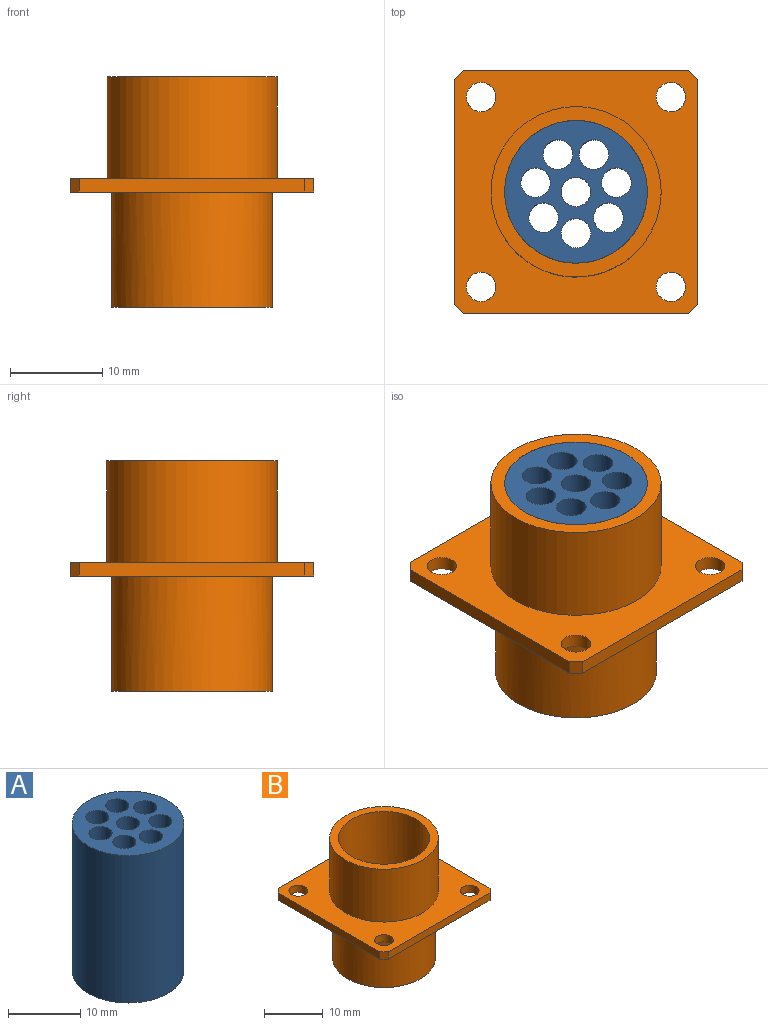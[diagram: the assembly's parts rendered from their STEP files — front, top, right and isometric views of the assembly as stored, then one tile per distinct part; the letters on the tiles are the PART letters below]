
ASSEMBLY  parts=2 mates=1
PART A: 11 faces, bbox 15.5x15.5x25 mm
  f0: cylinder r=7.75mm len=25mm, axis (0,0,1), area 1217.4mm2, adj f1,f10
  f1: plane 15.5x15.5mm, normal (0,0,-1), area 124.4mm2, adj f0,f2,f3,f4,f5,f6,f7,f8
  f2: cylinder r=1.6mm len=25mm, axis (0,0,1), area 251.3mm2, adj f1,f10
  f3: cylinder r=1.6mm len=25mm, axis (0,0,1), area 251.3mm2, adj f1,f10
  f4: cylinder r=1.6mm len=25mm, axis (0,0,1), area 251.3mm2, adj f1,f10
  f5: cylinder r=1.6mm len=25mm, axis (0,0,1), area 251.3mm2, adj f1,f10
  f6: cylinder r=1.6mm len=25mm, axis (0,0,1), area 251.3mm2, adj f1,f10
  f7: cylinder r=1.6mm len=25mm, axis (0,0,1), area 251.3mm2, adj f1,f10
  f8: cylinder r=1.6mm len=25mm, axis (0,0,1), area 251.3mm2, adj f1,f10
  f9: cylinder r=1.6mm len=25mm, axis (0,0,1), area 251.3mm2, adj f1,f10
  f10: plane 15.5x15.5mm, normal (0,0,1), area 124.4mm2, adj f0,f2,f3,f4,f5,f6,f7,f8
PART B: 19 faces, bbox 26.5x26.5x25 mm
  f0: plane 26.5x26.5mm, normal (0,0,-1), area 427.6mm2, adj f2,f3,f4,f5,f6,f7,f8,f9
  f1: plane 26.5x26.5mm, normal (0,0,1), area 399.3mm2, adj f2,f3,f4,f5,f6,f7,f8,f9
  f2: plane 24.5x1.5mm, normal (0,1,0), area 36.8mm2, adj f0,f1,f3,f9
  f3: plane 1.5x1mm, normal (0.71,0.71,0), area 2.1mm2, adj f0,f1,f2,f4
  f4: plane 24.5x1.5mm, normal (1,0,0), area 36.8mm2, adj f0,f1,f3,f5
  f5: plane 1.5x1mm, normal (0.71,-0.71,0), area 2.1mm2, adj f0,f1,f4,f6
  f6: plane 24.5x1.5mm, normal (0,-1,0), area 36.8mm2, adj f0,f1,f5,f7
  f7: plane 1.5x1mm, normal (-0.71,-0.71,0), area 2.1mm2, adj f0,f1,f6,f8
  f8: plane 24.5x1.5mm, normal (-1,0,0), area 36.8mm2, adj f0,f1,f7,f9
  f9: plane 1.5x1mm, normal (-0.71,0.71,0), area 2.1mm2, adj f0,f1,f2,f8
  f10: plane 18.5x18.5mm, normal (0,0,1), area 80.1mm2, adj f11,f12
  f11: cylinder r=9.25mm len=18.5mm, axis (0,0,-1), area 639.3mm2, adj f1,f10
  f12: cylinder r=7.75mm len=25mm, axis (0,0,-1), area 1217.4mm2, adj f10,f13
  f13: plane 17.5x17.5mm, normal (0,0,-1), area 51.8mm2, adj f12,f14
  f14: cylinder r=8.75mm len=17.5mm, axis (0,0,1), area 687.2mm2, adj f0,f13
  f15: cylinder r=1.6mm len=3.2mm, axis (0,0,-1), area 15.1mm2, adj f0,f1
  f16: cylinder r=1.6mm len=3.2mm, axis (0,0,-1), area 15.1mm2, adj f0,f1
  f17: cylinder r=1.6mm len=3.2mm, axis (0,0,-1), area 15.1mm2, adj f0,f1
  f18: cylinder r=1.6mm len=3.2mm, axis (0,0,-1), area 15.1mm2, adj f0,f1
PLACE A t=(0,0,8)mm
PLACE B at identity fixed
MATE fastened A.f0 <-> B.f11  axis (0,0,1) through (0,0,11)mm
